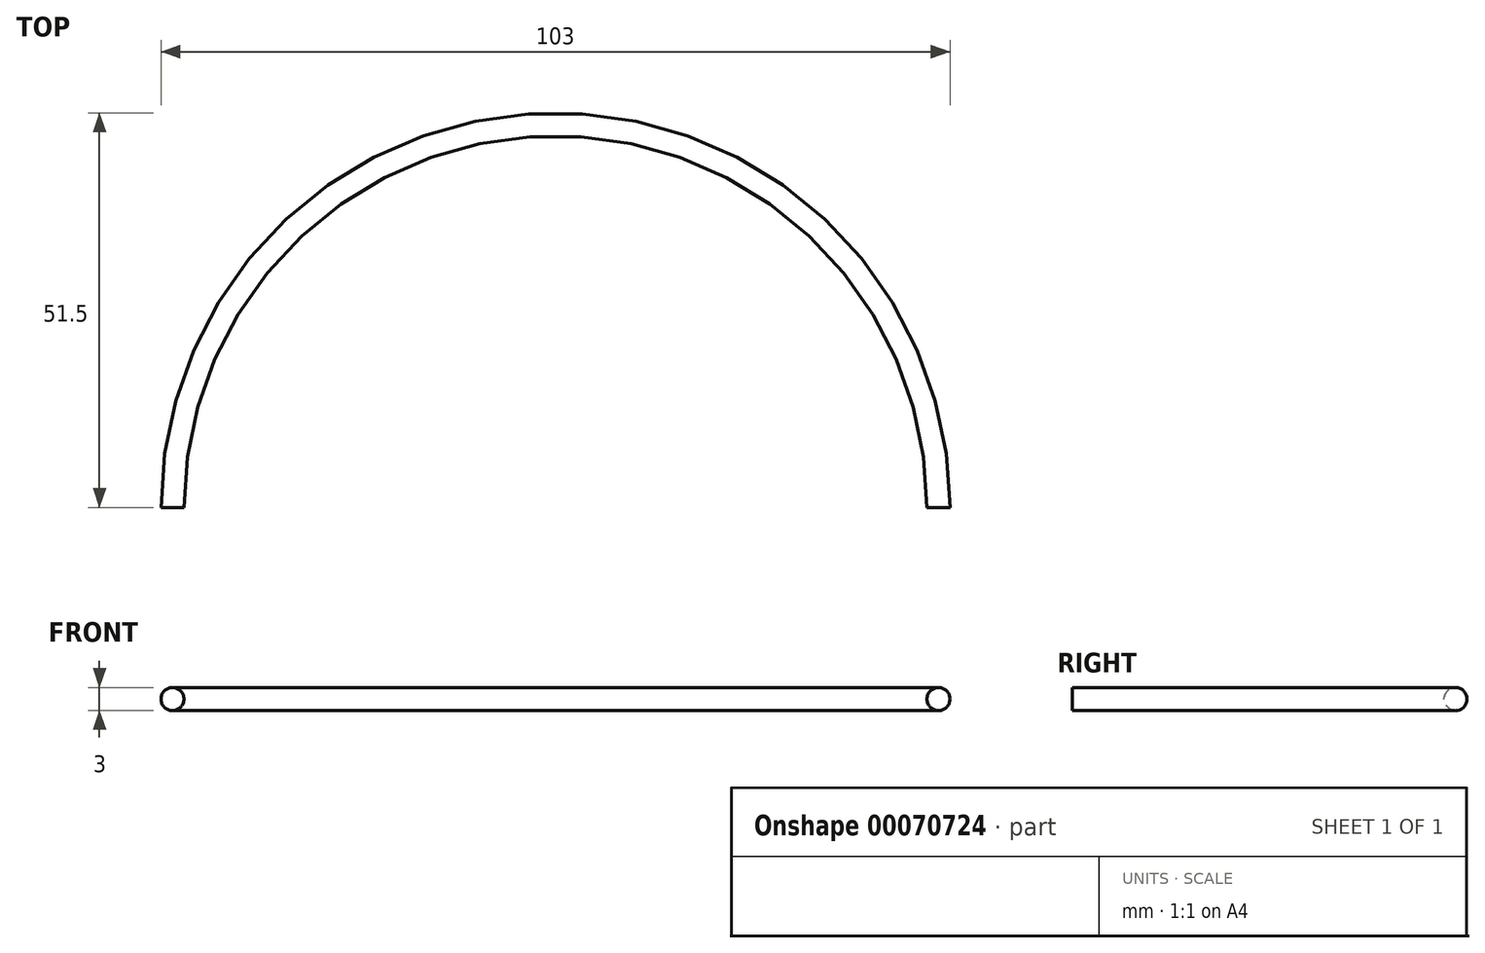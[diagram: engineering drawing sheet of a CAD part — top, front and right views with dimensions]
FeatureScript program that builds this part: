
annotation { "Feature Type Name" : "Feature", "Feature Type Description" : "" }
export const myFeature = defineFeature(function(context is Context, id is Id, definition is map)
    precondition{}
    {
        {
            var Q0;
            Q0=qCreatedBy(makeId("Top.planeOp"),FACE);
            var sketch = newSketch(context, id + "F0", { "sketchPlane" : qUnion([Q0])});
            skArc(sketch, "E0", {"start": v(-50, 0) * mm, "mid": v(0, 50) * mm, "end": v(50, 0) * mm});
            skSolve(sketch);
        }
        {
            var Q0;
            Q0=qCreatedBy(makeId("Front.planeOp"),FACE);
            var sketch = newSketch(context, id + "F1", { "sketchPlane" : qUnion([Q0])});
            skCircle(sketch, "E1", {"center": v(-50, 0) * mm, "radius": 1.5 * mm});
            skSolve(sketch);
        }
        {
            var Q0;
            Q0=makeQuery(id+"F1.imprint","IMPRINT",FACE,{"disambiguationData":[TD([[makeQuery(id+"F1.imprint","IMPRINT",EDGE,{"derivedFrom":sQuery(id+"F1.wireOp",EDGE,"E1")}),1.0]])]});
            var Q1;
            Q1=sQuery(id+"F0.wireOp",EDGE,"E0");
            sweep(context, id + "F2", {"profiles" : qUnion([Q0]), "path" : qUnion([Q1])});
        }
    });
